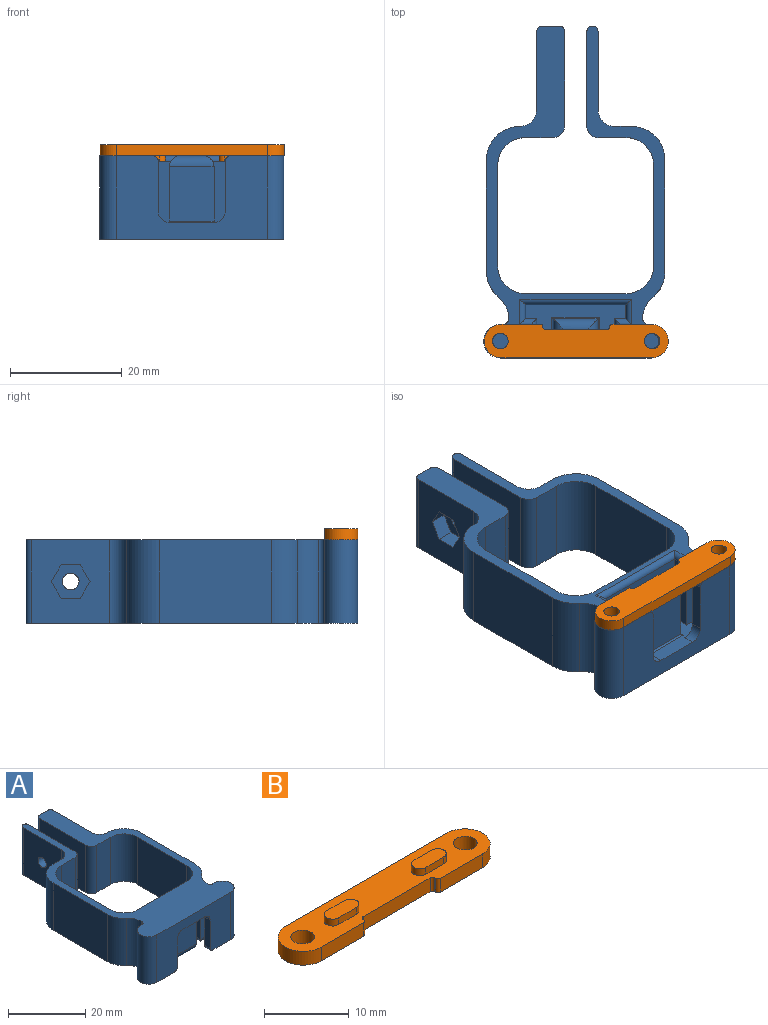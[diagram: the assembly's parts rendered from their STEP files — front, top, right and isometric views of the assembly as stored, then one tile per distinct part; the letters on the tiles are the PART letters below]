
ASSEMBLY  parts=2 mates=1
PART A: 103 faces, bbox 33x59.5x15 mm
  f0: plane 18x11mm, normal (0,-1,0), area 186mm2, adj f43,f52,f53,f86,f98,f99,f100,f101
  f1: cylinder r=1.4mm len=14mm, axis (0,0,1), area 123.2mm2, adj f24,f97
  f2: cylinder r=1.4mm len=14mm, axis (0,0,1), area 123.2mm2, adj f24,f96
  f3: cylinder r=6mm len=15mm, axis (0,0,-1), area 79.3mm2, adj f7,f23,f24,f66
  f4: plane 15x0.01mm, normal (-1,0,0), area 0.2mm2, adj f23,f24,f66,f95
  f5: cylinder r=6mm len=15mm, axis (0,0,-1), area 79.3mm2, adj f8,f23,f24,f67
  f6: plane 15x3mm, normal (0,1,0), area 45mm2, adj f23,f24,f25,f30
  f7: plane 20x15mm, normal (-1,0,0), area 300mm2, adj f3,f23,f24,f25
  f8: plane 20x15mm, normal (1,0,0), area 300mm2, adj f5,f23,f24,f26
  f9: plane 15x14mm, normal (1,0,0), area 178.8mm2, adj f23,f24,f29,f32,f34,f35,f36,f37
  f10: plane 15x3mm, normal (0,1,0), area 45mm2, adj f23,f24,f32,f33
  f11: plane 17x15mm, normal (-1,0,0), area 247.9mm2, adj f23,f24,f28,f33,f41
  f12: plane 15x5mm, normal (0,-1,0), area 75mm2, adj f13,f23,f24,f28
  f13: cylinder r=5mm len=15mm, axis (0,0,-1), area 117.8mm2, adj f12,f14,f23,f24
  f14: plane 18x15mm, normal (-1,0,0), area 270mm2, adj f13,f15,f23,f24
  f15: cylinder r=5mm len=15mm, axis (0,0,-1), area 117.8mm2, adj f14,f16,f23,f24
  f16: plane 18x15mm, normal (0,1,0), area 270mm2, adj f15,f17,f23,f24
  f17: cylinder r=5mm len=15mm, axis (0,0,-1), area 117.8mm2, adj f16,f18,f23,f24
  f18: plane 18x15mm, normal (1,0,0), area 270mm2, adj f17,f19,f23,f24
  f19: cylinder r=5mm len=15mm, axis (0,0,-1), area 117.8mm2, adj f18,f20,f23,f24
  f20: plane 15x5mm, normal (0,-1,0), area 75mm2, adj f19,f23,f24,f27
  f21: plane 17x15mm, normal (1,0,0), area 247.9mm2, adj f23,f24,f27,f31,f42
  f22: plane 15x14mm, normal (-1,0,0), area 202.9mm2, adj f23,f24,f30,f31,f42
  f23: plane 59.5x33mm, normal (0,0,1), area 627.1mm2, adj f3,f4,f5,f6,f7,f8,f9,f10
  f24: plane 59.5x33mm, normal (0,0,-1), area 403.8mm2, adj f1,f2,f3,f4,f5,f6,f7,f8
  f25: cylinder r=6mm len=15mm, axis (0,0,-1), area 141.4mm2, adj f6,f7,f23,f24
  f26: cylinder r=6mm len=15mm, axis (0,0,-1), area 141.4mm2, adj f8,f23,f24,f29
  f27: cylinder r=2mm len=15mm, axis (0,0,-1), area 47.1mm2, adj f20,f21,f23,f24
  f28: cylinder r=2mm len=15mm, axis (0,0,1), area 47.1mm2, adj f11,f12,f23,f24
  f29: cylinder r=3mm len=15mm, axis (0,0,-1), area 70.7mm2, adj f9,f23,f24,f26
  f30: cylinder r=3mm len=15mm, axis (0,0,1), area 70.7mm2, adj f6,f22,f23,f24
  f31: cylinder r=1mm len=15mm, axis (0,0,-1), area 47.1mm2, adj f21,f22,f23,f24
  f32: cylinder r=1mm len=15mm, axis (0,0,1), area 23.6mm2, adj f9,f10,f23,f24
  f33: cylinder r=1mm len=15mm, axis (0,0,-1), area 23.6mm2, adj f10,f11,f23,f24
  f34: plane 3x3mm, normal (0,-0.87,-0.5), area 10.4mm2, adj f9,f35,f39,f40
  f35: plane 3.46x3mm, normal (0,0,-1), area 10.4mm2, adj f9,f34,f36,f40
  f36: plane 3x3mm, normal (0,0.87,-0.5), area 10.4mm2, adj f9,f35,f37,f40
  f37: plane 3x3mm, normal (0,0.87,0.5), area 10.4mm2, adj f9,f36,f38,f40
  f38: plane 3.46x3mm, normal (0,0,1), area 10.4mm2, adj f9,f37,f39,f40
  f39: plane 3x3mm, normal (0,-0.87,0.5), area 10.4mm2, adj f9,f34,f38,f40
  f40: plane 6.93x6mm, normal (1,0,0), area 24.1mm2, adj f34,f35,f36,f37,f38,f39,f41
  f41: cylinder r=1.5mm len=3mm, axis (1,0,0), area 18.8mm2, adj f11,f40
  f42: cylinder r=1.5mm len=3mm, axis (1,0,0), area 18.8mm2, adj f21,f22
  f43: plane 20x9.5mm, normal (0,0,-1), area 106.4mm2, adj f0,f45,f46,f47,f48,f49,f50,f52
  f44: plane 15x0.01mm, normal (1,0,0), area 0.2mm2, adj f23,f24,f67,f94
  f45: plane 27x15mm, normal (0,-1,0), area 262.3mm2, adj f23,f24,f43,f51,f59,f64,f65,f74
  f46: plane 11x2mm, normal (0,1,0), area 22mm2, adj f43,f47,f52,f84
  f47: plane 11x2.5mm, normal (-1,0,0), area 27.5mm2, adj f43,f46,f48,f83
  f48: plane 11x3mm, normal (0,-1,0), area 33mm2, adj f43,f47,f49,f82
  f49: plane 11x2.5mm, normal (-1,0,0), area 27.5mm2, adj f43,f48,f50,f81
  f50: plane 11x6mm, normal (0,1,0), area 44.9mm2, adj f43,f49,f51,f65,f80
  f51: plane 9x2mm, normal (-1,0,0), area 18mm2, adj f45,f50,f65,f79
  f52: plane 11x2.5mm, normal (-1,0,0), area 27.5mm2, adj f0,f43,f46,f85
  f53: plane 11x2.5mm, normal (1,0,0), area 27.5mm2, adj f0,f43,f54,f87
  f54: plane 11x2mm, normal (0,1,0), area 22mm2, adj f43,f53,f55,f88
  f55: plane 11x2.5mm, normal (1,0,0), area 27.5mm2, adj f43,f54,f56,f89
  f56: plane 11x3mm, normal (0,-1,0), area 33mm2, adj f43,f55,f57,f90
  f57: plane 11x2.5mm, normal (1,0,0), area 27.5mm2, adj f43,f56,f58,f92
  f58: plane 11x6mm, normal (0,1,0), area 44.9mm2, adj f43,f57,f59,f64,f93
  f59: plane 9x2mm, normal (1,0,0), area 18mm2, adj f45,f58,f64,f91
  f60: plane 9.7x8mm, normal (0,1,0), area 77.6mm2, adj f61,f63,f68,f76
  f61: plane 9.7x4mm, normal (1,0,0), area 38.8mm2, adj f60,f62,f70,f78
  f62: plane 9.7x8mm, normal (0,-1,0), area 77.6mm2, adj f61,f63,f71,f76
  f63: plane 9.7x4mm, normal (-1,0,0), area 38.8mm2, adj f60,f62,f69,f77
  f64: cylinder r=2mm len=2mm, axis (0,1,0), area 6.3mm2, adj f43,f45,f58,f59
  f65: cylinder r=2mm len=2mm, axis (0,-1,0), area 6.3mm2, adj f43,f45,f50,f51
  f66: cylinder r=5mm len=15mm, axis (0,0,-1), area 66.1mm2, adj f3,f4,f23,f24
  f67: cylinder r=5mm len=15mm, axis (0,0,-1), area 66.1mm2, adj f5,f23,f24,f44
  f68: cylinder r=0.3mm len=8.6mm, axis (-1,0,0), area 3.9mm2, adj f43,f60,f69,f70
  f69: cylinder r=0.3mm len=4.6mm, axis (0,-1,0), area 2mm2, adj f43,f63,f68,f71
  f70: cylinder r=0.3mm len=4.6mm, axis (0,1,0), area 2mm2, adj f43,f61,f68,f71
  f71: cylinder r=0.3mm len=8.6mm, axis (1,0,0), area 3.9mm2, adj f43,f62,f69,f70
  f72: plane 15x0.5mm, normal (0,1,0), area 7.5mm2, adj f23,f24,f75,f95
  f73: plane 15x0.5mm, normal (0,1,0), area 7.5mm2, adj f23,f24,f74,f94
  f74: cylinder r=3mm len=15mm, axis (0,0,-1), area 141.4mm2, adj f23,f24,f45,f73
  f75: cylinder r=3mm len=15mm, axis (0,0,1), area 141.4mm2, adj f23,f24,f45,f72
  f76: cylinder r=2mm len=8mm, axis (-1,0,0), area 41.1mm2, adj f60,f62,f77,f78
  f77: cylinder r=2mm len=4mm, axis (0,-1,0), area 8mm2, adj f63,f76
  f78: cylinder r=2mm len=4mm, axis (0,1,0), area 8mm2, adj f61,f76
  f79: cylinder r=1mm len=2mm, axis (0,1,0), area 2.6mm2, adj f24,f45,f51,f80
  f80: cylinder r=1mm len=5mm, axis (1,0,0), area 6.3mm2, adj f24,f50,f79,f81
  f81: cylinder r=1mm len=4.5mm, axis (0,1,0), area 5.1mm2, adj f24,f49,f80,f82
  f82: cylinder r=1mm len=4mm, axis (-1,0,0), area 4.7mm2, adj f24,f48,f81,f83
  f83: cylinder r=1mm len=2.5mm, axis (0,1,0), area 2.8mm2, adj f24,f47,f82,f84
  f84: cylinder r=1mm len=3mm, axis (1,0,0), area 3.1mm2, adj f24,f46,f83,f85
  f85: cylinder r=1mm len=4.5mm, axis (0,1,0), area 5.1mm2, adj f24,f52,f84,f86
  f86: cylinder r=1mm len=20mm, axis (1,0,0), area 29.4mm2, adj f0,f24,f85,f87
  f87: cylinder r=1mm len=4.5mm, axis (0,-1,0), area 5.1mm2, adj f24,f53,f86,f88
  f88: cylinder r=1mm len=3mm, axis (1,0,0), area 3.1mm2, adj f24,f54,f87,f89
  f89: cylinder r=1mm len=2.5mm, axis (0,-1,0), area 2.8mm2, adj f24,f55,f88,f90
  f90: cylinder r=1mm len=4mm, axis (-1,0,0), area 4.7mm2, adj f24,f56,f89,f92
  f91: cylinder r=1mm len=2mm, axis (0,-1,0), area 2.6mm2, adj f24,f45,f59,f93
  f92: cylinder r=1mm len=4.5mm, axis (0,-1,0), area 5.1mm2, adj f24,f57,f90,f93
  f93: cylinder r=1mm len=5mm, axis (1,0,0), area 6.3mm2, adj f24,f58,f91,f92
  f94: cylinder r=1mm len=15mm, axis (0,0,-1), area 23.6mm2, adj f23,f24,f44,f73
  f95: cylinder r=1mm len=15mm, axis (0,0,1), area 23.6mm2, adj f4,f23,f24,f72
  f96: plane 2.8x2.8mm, normal (0,0,-1), area 6.2mm2, adj f2
  f97: plane 2.8x2.8mm, normal (0,0,-1), area 6.2mm2, adj f1
  f98: plane 6x1mm, normal (0,0,-1), area 6mm2, adj f0,f99,f101,f102
  f99: plane 2x1mm, normal (1,0,0), area 2mm2, adj f0,f98,f100,f102
  f100: plane 6x1mm, normal (0,0,1), area 6mm2, adj f0,f99,f101,f102
  f101: plane 2x1mm, normal (-1,0,0), area 2mm2, adj f0,f98,f100,f102
  f102: plane 6x2mm, normal (0,-1,0), area 12mm2, adj f98,f99,f100,f101
PART B: 26 faces, bbox 33x6x3 mm
  f0: plane 33x6mm, normal (0,0,1), area 148.9mm2, adj f1,f2,f3,f4,f5,f6,f7,f8
  f1: plane 27x2mm, normal (0,1,0), area 54mm2, adj f0,f9,f16,f17
  f2: plane 7.1x2mm, normal (0,-1,0), area 14.2mm2, adj f0,f9,f16,f22
  f3: plane 2x0.1mm, normal (1,0,0), area 0.2mm2, adj f0,f9,f22,f23
  f4: plane 11.2x2mm, normal (0,-1,0), area 22.4mm2, adj f0,f9,f23,f24
  f5: plane 2x0.1mm, normal (-1,0,0), area 0.2mm2, adj f0,f9,f24,f25
  f6: plane 7.1x2mm, normal (0,-1,0), area 14.2mm2, adj f0,f9,f17,f25
  f7: cylinder r=1.4mm len=2.8mm, axis (0,0,-1), area 17.6mm2, adj f0,f9
  f8: cylinder r=1.4mm len=2.8mm, axis (0,0,-1), area 17.6mm2, adj f0,f9
  f9: plane 33x6mm, normal (0,0,-1), area 167.2mm2, adj f1,f2,f3,f4,f5,f6,f7,f8
  f10: plane 3x1mm, normal (0,1,0), area 3mm2, adj f0,f12,f20,f21
  f11: plane 3x1mm, normal (0,-1,0), area 3mm2, adj f0,f12,f20,f21
  f12: plane 5x2mm, normal (0,0,1), area 9.1mm2, adj f10,f11,f20,f21
  f13: plane 3x1mm, normal (0,1,0), area 3mm2, adj f0,f15,f18,f19
  f14: plane 3x1mm, normal (0,-1,0), area 3mm2, adj f0,f15,f18,f19
  f15: plane 5x2mm, normal (0,0,1), area 9.1mm2, adj f13,f14,f18,f19
  f16: cylinder r=3mm len=6mm, axis (0,0,-1), area 18.8mm2, adj f0,f1,f2,f9
  f17: cylinder r=3mm len=6mm, axis (0,0,-1), area 18.8mm2, adj f0,f1,f6,f9
  f18: cylinder r=1mm len=2mm, axis (0,0,-1), area 3.1mm2, adj f0,f13,f14,f15
  f19: cylinder r=1mm len=2mm, axis (0,0,-1), area 3.1mm2, adj f0,f13,f14,f15
  f20: cylinder r=1mm len=2mm, axis (0,0,-1), area 3.1mm2, adj f0,f10,f11,f12
  f21: cylinder r=1mm len=2mm, axis (0,0,-1), area 3.1mm2, adj f0,f10,f11,f12
  f22: cylinder r=0.4mm len=2mm, axis (0,0,1), area 1.3mm2, adj f0,f2,f3,f9
  f23: cylinder r=0.4mm len=2mm, axis (0,0,1), area 1.3mm2, adj f0,f3,f4,f9
  f24: cylinder r=0.4mm len=2mm, axis (0,0,1), area 1.3mm2, adj f0,f4,f5,f9
  f25: cylinder r=0.4mm len=2mm, axis (0,0,1), area 1.3mm2, adj f0,f5,f6,f9
PLACE A rot(axis=(0,1,0),180deg) t=(-30.15,-2.28,25.89)mm
PLACE B rot(axis=(1,0,0),180deg) t=(37.95,12.74,27.89)mm
MATE fastened A.f1 <-> B.f8  axis (0,0,1) through (-4.92,9.74,25.89)mm
